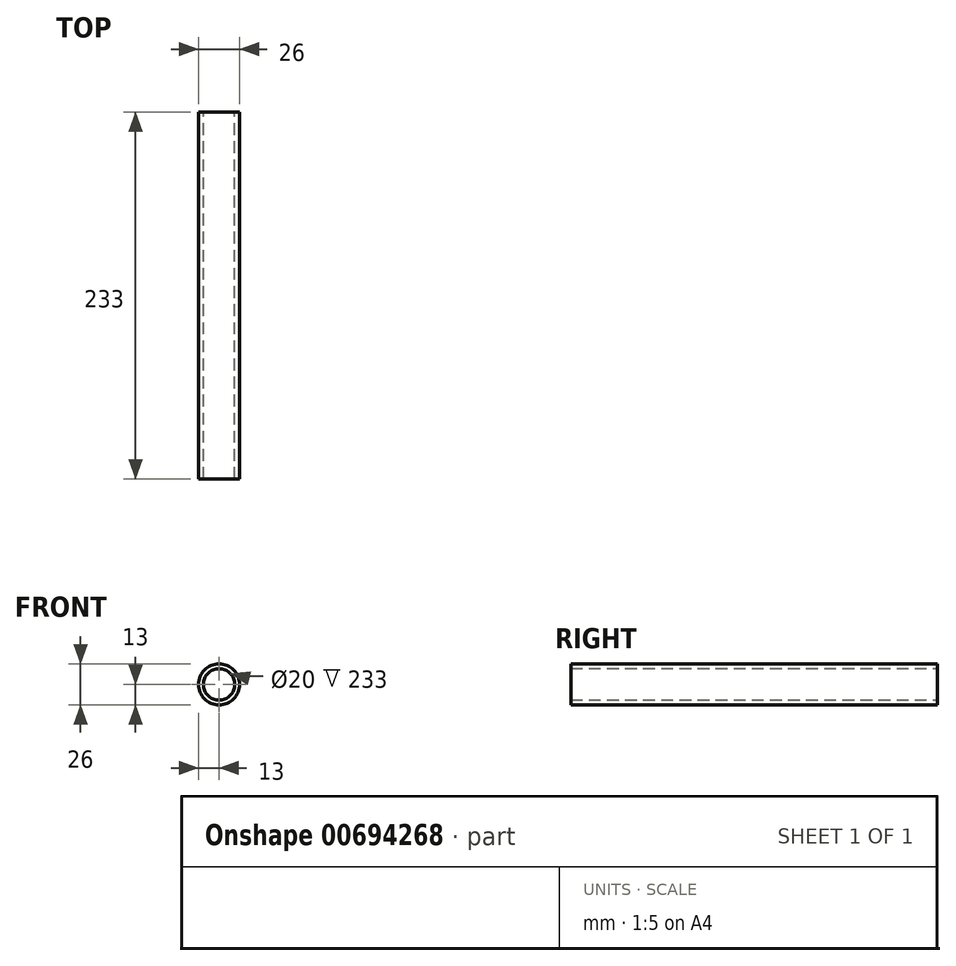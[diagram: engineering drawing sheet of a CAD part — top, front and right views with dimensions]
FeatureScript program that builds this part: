
annotation { "Feature Type Name" : "Feature", "Feature Type Description" : "" }
export const myFeature = defineFeature(function(context is Context, id is Id, definition is map)
    precondition{}
    {
        {
            var Q0;
            Q0=qCreatedBy(makeId("Front.planeOp"),FACE);
            var sketch = newSketch(context, id + "F0", { "sketchPlane" : qUnion([Q0])});
            skCircle(sketch, "E0", {"center": v(0, 0) * mm, "radius": 10 * mm});
            skCircle(sketch, "E1", {"center": v(0, 0) * mm, "radius": 13 * mm});
            skSolve(sketch);
        }
        {
            var Q0;
            Q0=qSketchRegion(id+"F0",true);
            extrude(context, id + "F1", {"entities" : qUnion([Q0]), "depth" : (200 + 33) * mm, "offsetDistance" : 25 * mm});
        }
    });
